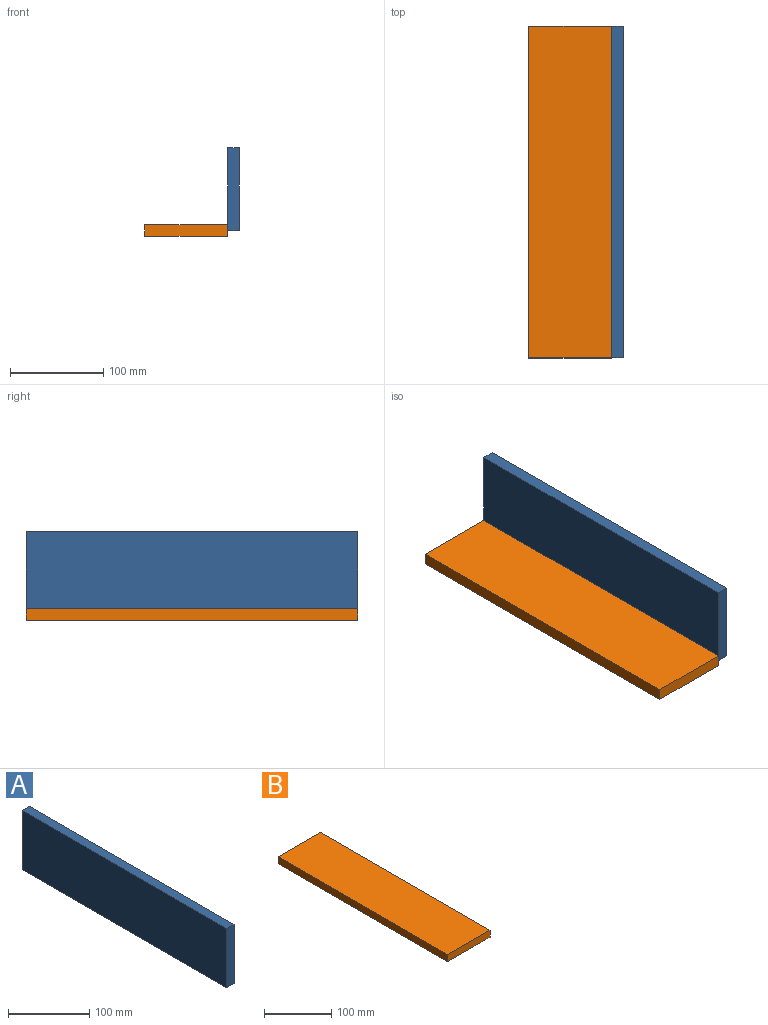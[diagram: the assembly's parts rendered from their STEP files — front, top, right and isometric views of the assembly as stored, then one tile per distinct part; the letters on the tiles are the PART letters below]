
ASSEMBLY  parts=2 mates=1
PART A: 6 faces, bbox 12.7x355.6x88.9 mm
  f0: plane 88.9x12.7mm, normal (0,1,0), area 1129mm2, adj f1,f3,f4,f5
  f1: plane 355.6x12.7mm, normal (0,0,1), area 4516.1mm2, adj f0,f2,f4,f5
  f2: plane 88.9x12.7mm, normal (0,-1,0), area 1129mm2, adj f1,f3,f4,f5
  f3: plane 355.6x12.7mm, normal (0,0,-1), area 4516.1mm2, adj f0,f2,f4,f5
  f4: plane 355.6x88.9mm, normal (1,0,0), area 31612.8mm2, adj f0,f1,f2,f3
  f5: plane 355.6x88.9mm, normal (-1,0,0), area 31612.8mm2, adj f0,f1,f2,f3
PART B: 6 faces, bbox 88.9x355.6x12.7 mm
  f0: plane 88.9x12.7mm, normal (0,-1,0), area 1129mm2, adj f1,f3,f4,f5
  f1: plane 355.6x12.7mm, normal (1,0,0), area 4516.1mm2, adj f0,f2,f4,f5
  f2: plane 88.9x12.7mm, normal (0,1,0), area 1129mm2, adj f1,f3,f4,f5
  f3: plane 355.6x12.7mm, normal (-1,0,0), area 4516.1mm2, adj f0,f2,f4,f5
  f4: plane 355.6x88.9mm, normal (0,0,1), area 31612.8mm2, adj f0,f1,f2,f3
  f5: plane 355.6x88.9mm, normal (0,0,-1), area 31612.8mm2, adj f0,f1,f2,f3
PLACE A t=(44.45,0,50.8)mm
PLACE B at identity
MATE planar A.f5 <-> B.f1  axis (-1,0,0) through (44.45,0,6.35)mm
